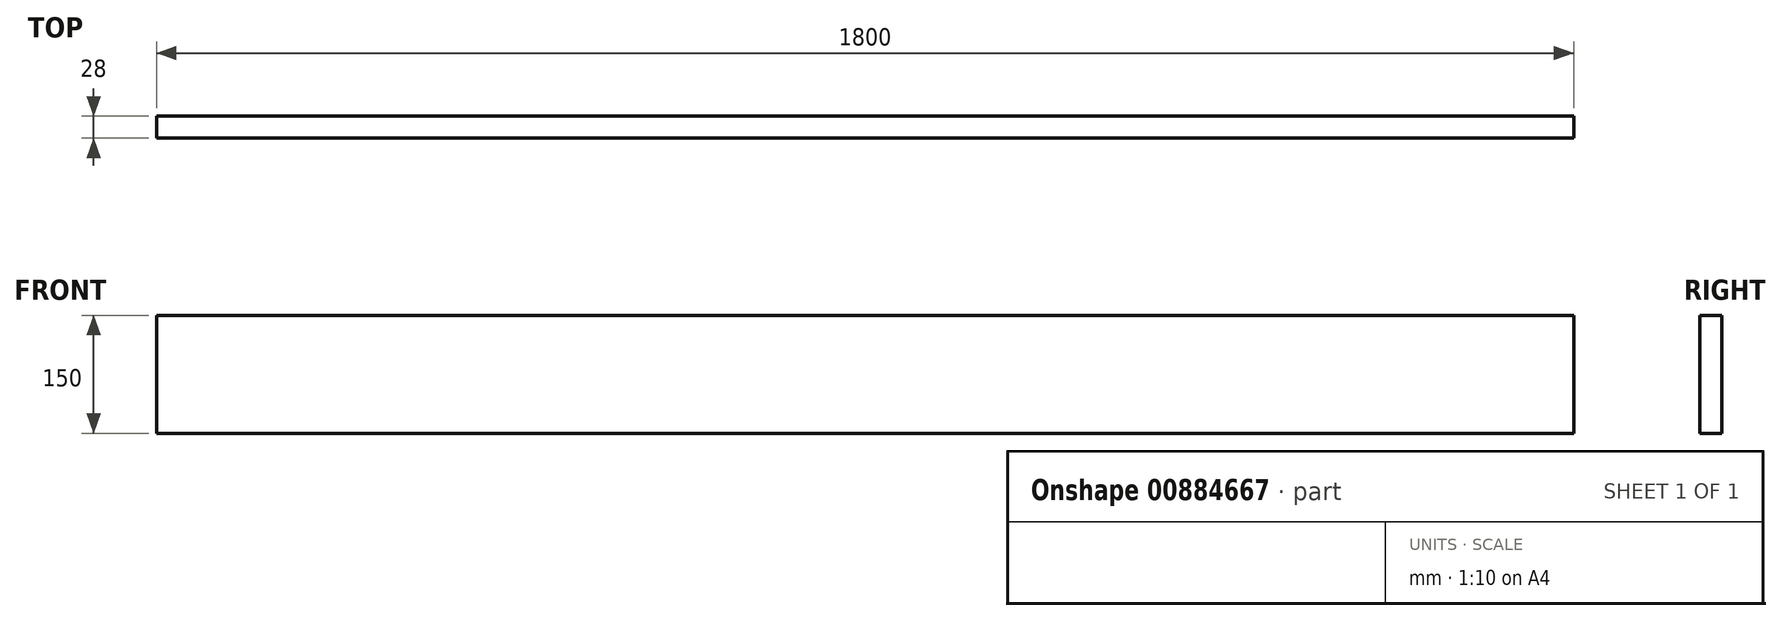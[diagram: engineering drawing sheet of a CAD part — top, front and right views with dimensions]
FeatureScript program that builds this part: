
annotation { "Feature Type Name" : "Feature", "Feature Type Description" : "" }
export const myFeature = defineFeature(function(context is Context, id is Id, definition is map)
    precondition{}
    {
        {
            var Q0;
            Q0=qCreatedBy(makeId("Front.planeOp"),FACE);
            var sketch = newSketch(context, id + "F0", { "sketchPlane" : qUnion([Q0])});
            skLineSegment(sketch, "E0.bottom", {"start": v(0, 0) * mm, "end": v(1800, 0) * mm});
            skLineSegment(sketch, "E0.top", {"start": v(0, 150) * mm, "end": v(1800, 150) * mm});
            skLineSegment(sketch, "E0.left", {"start": v(0, 0) * mm, "end": v(0, 150) * mm});
            skLineSegment(sketch, "E0.right", {"start": v(1800, 0) * mm, "end": v(1800, 150) * mm});
            skSolve(sketch);
        }
        {
            var Q0;
            Q0 = qSketchRegion(id + "F0", true);
            extrude(context, id + "F1", {"entities" : qUnion([Q0]), "depth" : 28 * mm, "offsetDistance" : 25 * mm});
        }
    });
